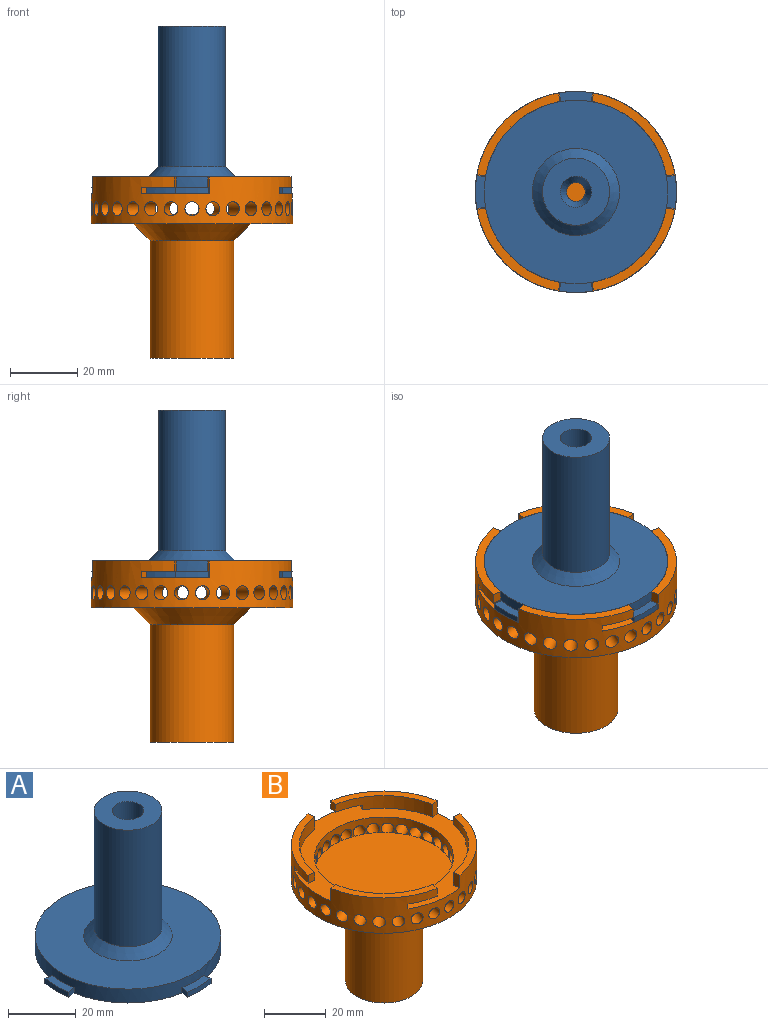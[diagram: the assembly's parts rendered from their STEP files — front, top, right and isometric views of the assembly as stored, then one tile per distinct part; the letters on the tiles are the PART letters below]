
ASSEMBLY  parts=2 mates=1
PART A: 27 faces, bbox 60x60x52.4 mm
  f0: plane 54.7x54.7mm, normal (0,0,1), area 1819.1mm2, adj f1,f26
  f1: cylinder r=27.35mm len=54.7mm, axis (0,0,-1), area 792.1mm2, adj f0,f9,f10,f11,f13,f15,f16,f17
  f2: cylinder r=4.65mm len=43.6mm, axis (0,0,-1), area 1273.7mm2, adj f4,f8
  f3: cylinder r=10mm len=42mm, axis (0,0,-1), area 2638.9mm2, adj f4,f26
  f4: plane 20x20mm, normal (0,0,1), area 246.2mm2, adj f2,f3
  f5: cylinder r=22.45mm len=44.9mm, axis (0,0,1), area 338.5mm2, adj f6,f9
  f6: plane 44.9x44.9mm, normal (0,0,-1), area 1558.7mm2, adj f5,f7
  f7: cylinder r=2.8mm len=5.6mm, axis (0,0,-1), area 80.9mm2, adj f6,f8
  f8: cone r=5mm half-angle=23.7deg, axis (0,0,1), area 107.5mm2, adj f2,f7
  f9: plane 60x60mm, normal (0,0,-1), area 867.4mm2, adj f1,f5,f10,f11,f12,f13,f14,f15
  f10: plane 2.61x1.85mm, normal (-0.17,0.99,0), area 4.9mm2, adj f1,f9,f12,f25
  f11: plane 2.61x1.85mm, normal (-0.17,-0.99,0), area 4.9mm2, adj f1,f9,f12,f25
  f12: cylinder r=30mm len=9.9mm, axis (0,0,1), area 18.4mm2, adj f9,f10,f11,f25
  f13: plane 2.61x1.85mm, normal (0.99,-0.17,0), area 4.9mm2, adj f1,f9,f14,f24
  f14: cylinder r=30mm len=9.9mm, axis (0,0,1), area 18.4mm2, adj f9,f13,f15,f24
  f15: plane 2.61x1.85mm, normal (-0.99,-0.17,0), area 4.9mm2, adj f1,f9,f14,f24
  f16: plane 2.61x1.85mm, normal (0.17,-0.99,0), area 4.9mm2, adj f1,f9,f18,f23
  f17: plane 2.61x1.85mm, normal (0.17,0.99,0), area 4.9mm2, adj f1,f9,f18,f23
  f18: cylinder r=30mm len=9.9mm, axis (0,0,1), area 18.4mm2, adj f9,f16,f17,f23
  f19: plane 2.61x1.85mm, normal (-0.99,0.17,0), area 4.9mm2, adj f1,f9,f20,f22
  f20: cylinder r=30mm len=9.9mm, axis (0,0,1), area 18.4mm2, adj f9,f19,f21,f22
  f21: plane 2.61x1.85mm, normal (0.99,0.17,0), area 4.9mm2, adj f1,f9,f20,f22
  f22: plane 9.9x3.03mm, normal (0,0,1), area 25.2mm2, adj f1,f19,f20,f21
  f23: plane 9.9x3.03mm, normal (0,0,1), area 25.2mm2, adj f1,f16,f17,f18
  f24: plane 9.9x3.03mm, normal (0,0,1), area 25.2mm2, adj f1,f13,f14,f15
  f25: plane 9.9x3.03mm, normal (0,0,1), area 25.2mm2, adj f1,f10,f11,f12
  f26: cone r=10mm half-angle=45deg, axis (0,0,-1), area 306.6mm2, adj f0,f3
PART B: 94 faces, bbox 60.1x60x54 mm
  f0: cylinder r=30mm len=60mm, axis (0,0,-1), area 1933mm2, adj f5,f6,f7,f8,f10,f11,f12,f13
  f1: cylinder r=27.4mm len=22.23mm, axis (0,0,-1), area 149.2mm2, adj f5,f8,f77,f83,f87,f88
  f2: cylinder r=27.4mm len=22.23mm, axis (0,0,-1), area 149.2mm2, adj f6,f8,f80,f81,f85,f86
  f3: cylinder r=27.4mm len=22.23mm, axis (0,0,-1), area 149.2mm2, adj f7,f8,f79,f84,f91,f92
  f4: cylinder r=27.4mm len=22.23mm, axis (0,0,-1), area 149.2mm2, adj f8,f76,f78,f82,f89,f90
  f5: plane 24.79x24.79mm, normal (0,0,1), area 91.2mm2, adj f0,f1,f77,f83
  f6: plane 24.79x24.79mm, normal (0,0,1), area 91.2mm2, adj f0,f2,f80,f81
  f7: plane 24.79x24.79mm, normal (0,0,1), area 91.2mm2, adj f0,f3,f79,f84
  f8: plane 60x60mm, normal (0,0,1), area 976.5mm2, adj f0,f1,f2,f3,f4,f9,f78,f79
  f9: cylinder r=22.5mm len=45mm, axis (0,0,1), area 475mm2, adj f8,f10,f11,f12,f13,f14,f15,f16
  f10: cylinder r=2.1mm len=8.31mm, axis (-0.21,-0.98,0), area 99.1mm2, adj f0,f9,f45
  f11: cylinder r=2.1mm len=8.65mm, axis (-0.41,-0.91,0), area 99.1mm2, adj f0,f9,f46
  f12: cylinder r=2.1mm len=8.62mm, axis (-0.59,-0.81,0), area 99.1mm2, adj f0,f9,f47
  f13: cylinder r=2.1mm len=8.46mm, axis (-0.74,-0.67,0), area 99.1mm2, adj f0,f9,f48
  f14: cylinder r=2.1mm len=8.68mm, axis (-0.87,-0.5,0), area 99.1mm2, adj f0,f9,f49
  f15: cylinder r=2.1mm len=8.52mm, axis (-0.95,-0.31,0), area 99.1mm2, adj f0,f9,f50
  f16: cylinder r=2.1mm len=8mm, axis (-0.99,-0.1,0), area 99.1mm2, adj f0,f9,f51
  f17: cylinder r=2.1mm len=8mm, axis (-0.99,0.1,0), area 99.1mm2, adj f0,f9,f52
  f18: cylinder r=2.1mm len=8.52mm, axis (-0.95,0.31,0), area 99.1mm2, adj f0,f9,f53
  f19: cylinder r=2.1mm len=8.68mm, axis (-0.87,0.5,0), area 99.1mm2, adj f0,f9,f54
  f20: cylinder r=2.1mm len=8.46mm, axis (-0.74,0.67,0), area 99.1mm2, adj f0,f9,f55
  f21: cylinder r=2.1mm len=8.62mm, axis (-0.59,0.81,0), area 99.1mm2, adj f0,f9,f56
  f22: cylinder r=2.1mm len=8.65mm, axis (-0.41,0.91,0), area 99.1mm2, adj f0,f9,f57
  f23: cylinder r=2.1mm len=8.31mm, axis (-0.21,0.98,0), area 99.1mm2, adj f0,f9,f58
  f24: cylinder r=2.1mm len=7.6mm, axis (0,1,0), area 99.1mm2, adj f0,f9,f59
  f25: cylinder r=2.1mm len=8.31mm, axis (0.21,0.98,0), area 99.1mm2, adj f0,f9,f60
  f26: cylinder r=2.1mm len=8.65mm, axis (0.41,0.91,0), area 99.1mm2, adj f0,f9,f61
  f27: cylinder r=2.1mm len=8.62mm, axis (0.59,0.81,0), area 99.1mm2, adj f0,f9,f62
  f28: cylinder r=2.1mm len=8.46mm, axis (0.74,0.67,0), area 99.1mm2, adj f0,f9,f63
  f29: cylinder r=2.1mm len=8.68mm, axis (0.87,0.5,0), area 99.1mm2, adj f0,f9,f64
  f30: cylinder r=2.1mm len=8.52mm, axis (0.95,0.31,0), area 99.1mm2, adj f0,f9,f65
  f31: cylinder r=2.1mm len=8mm, axis (0.99,0.1,0), area 99.1mm2, adj f0,f9,f66
  f32: cylinder r=2.1mm len=8mm, axis (0.99,-0.1,0), area 99.1mm2, adj f0,f9,f67
  f33: cylinder r=2.1mm len=8.52mm, axis (0.95,-0.31,0), area 99.1mm2, adj f0,f9,f68
  f34: cylinder r=2.1mm len=8.68mm, axis (0.87,-0.5,0), area 99.1mm2, adj f0,f9,f69
  f35: cylinder r=2.1mm len=8.46mm, axis (0.74,-0.67,0), area 99.1mm2, adj f0,f9,f70
  f36: cylinder r=2.1mm len=8.62mm, axis (0.59,-0.81,0), area 99.1mm2, adj f0,f9,f71
  f37: cylinder r=2.1mm len=8.65mm, axis (0.41,-0.91,0), area 99.1mm2, adj f0,f9,f72
  f38: cylinder r=2.1mm len=8.31mm, axis (0.21,-0.98,0), area 99.1mm2, adj f0,f9,f73
  f39: cylinder r=4.1mm len=30mm, axis (0,0,-1), area 772.8mm2, adj f41,f42
  f40: cylinder r=12.5mm len=35mm, axis (0,0,-1), area 2748.9mm2, adj f41,f93
  f41: plane 25x25mm, normal (0,0,-1), area 438.1mm2, adj f39,f40
  f42: plane 8.2x8.2mm, normal (0,0,-1), area 52.8mm2, adj f39
  f43: plane 60x60mm, normal (0,0,-1), area 1865.3mm2, adj f0,f93
  f44: cylinder r=2.1mm len=7.6mm, axis (0,-1,0), area 99.1mm2, adj f0,f9,f74
  f45: cylinder r=22.5mm len=2.6mm, axis (0,0,-1), area 0.9mm2, adj f10,f75
  f46: cylinder r=22.5mm len=2.43mm, axis (0,0,-1), area 0.9mm2, adj f11,f75
  f47: cylinder r=22.5mm len=2.15mm, axis (0,0,-1), area 0.9mm2, adj f12,f75
  f48: cylinder r=22.5mm len=1.98mm, axis (0,0,-1), area 0.9mm2, adj f13,f75
  f49: cylinder r=22.5mm len=2.3mm, axis (0,0,-1), area 0.9mm2, adj f14,f75
  f50: cylinder r=22.5mm len=2.53mm, axis (0,0,-1), area 0.9mm2, adj f15,f75
  f51: cylinder r=22.5mm len=2.65mm, axis (0,0,-1), area 0.9mm2, adj f16,f75
  f52: cylinder r=22.5mm len=2.65mm, axis (0,0,-1), area 0.9mm2, adj f17,f75
  f53: cylinder r=22.5mm len=2.53mm, axis (0,0,-1), area 0.9mm2, adj f18,f75
  f54: cylinder r=22.5mm len=2.3mm, axis (0,0,-1), area 0.9mm2, adj f19,f75
  f55: cylinder r=22.5mm len=1.98mm, axis (0,0,-1), area 0.9mm2, adj f20,f75
  f56: cylinder r=22.5mm len=2.15mm, axis (0,0,-1), area 0.9mm2, adj f21,f75
  f57: cylinder r=22.5mm len=2.43mm, axis (0,0,-1), area 0.9mm2, adj f22,f75
  f58: cylinder r=22.5mm len=2.6mm, axis (0,0,-1), area 0.9mm2, adj f23,f75
  f59: cylinder r=22.5mm len=2.66mm, axis (0,0,-1), area 0.9mm2, adj f24,f75
  f60: cylinder r=22.5mm len=2.6mm, axis (0,0,-1), area 0.9mm2, adj f25,f75
  f61: cylinder r=22.5mm len=2.43mm, axis (0,0,-1), area 0.9mm2, adj f26,f75
  f62: cylinder r=22.5mm len=2.15mm, axis (0,0,-1), area 0.9mm2, adj f27,f75
  f63: cylinder r=22.5mm len=1.98mm, axis (0,0,-1), area 0.9mm2, adj f28,f75
  f64: cylinder r=22.5mm len=2.3mm, axis (0,0,-1), area 0.9mm2, adj f29,f75
  f65: cylinder r=22.5mm len=2.53mm, axis (0,0,-1), area 0.9mm2, adj f30,f75
  f66: cylinder r=22.5mm len=2.65mm, axis (0,0,-1), area 0.9mm2, adj f31,f75
  f67: cylinder r=22.5mm len=2.65mm, axis (0,0,-1), area 0.9mm2, adj f32,f75
  f68: cylinder r=22.5mm len=2.53mm, axis (0,0,-1), area 0.9mm2, adj f33,f75
  f69: cylinder r=22.5mm len=2.3mm, axis (0,0,-1), area 0.9mm2, adj f34,f75
  f70: cylinder r=22.5mm len=1.98mm, axis (0,0,-1), area 0.9mm2, adj f35,f75
  f71: cylinder r=22.5mm len=2.15mm, axis (0,0,-1), area 0.9mm2, adj f36,f75
  f72: cylinder r=22.5mm len=2.43mm, axis (0,0,-1), area 0.9mm2, adj f37,f75
  f73: cylinder r=22.5mm len=2.6mm, axis (0,0,-1), area 0.9mm2, adj f38,f75
  f74: cylinder r=22.5mm len=2.66mm, axis (0,0,-1), area 0.9mm2, adj f44,f75
  f75: plane 45x45mm, normal (0,0,1), area 1590.4mm2, adj f9,f45,f46,f47,f48,f49,f50,f51
  f76: plane 24.79x24.79mm, normal (0,0,1), area 91.2mm2, adj f0,f4,f78,f82
  f77: plane 3.1x2.56mm, normal (0.98,-0.17,0), area 8.1mm2, adj f0,f1,f5,f88
  f78: plane 5x2.56mm, normal (-0.98,-0.17,0), area 13mm2, adj f0,f4,f8,f76
  f79: plane 5x2.56mm, normal (0.98,0.17,0), area 13mm2, adj f0,f3,f7,f8
  f80: plane 3.1x2.56mm, normal (-0.98,0.17,0), area 8.1mm2, adj f0,f2,f6,f86
  f81: plane 5x2.56mm, normal (0.17,-0.98,0), area 13mm2, adj f0,f2,f6,f8
  f82: plane 3.1x2.56mm, normal (0.17,0.98,0), area 8.1mm2, adj f0,f4,f76,f90
  f83: plane 5x2.56mm, normal (-0.17,0.98,0), area 13mm2, adj f0,f1,f5,f8
  f84: plane 3.1x2.56mm, normal (-0.17,-0.98,0), area 8.1mm2, adj f0,f3,f7,f92
  f85: plane 2.25x1.9mm, normal (-0.87,0.5,0), area 4.9mm2, adj f0,f2,f8,f86
  f86: plane 10.24x5.82mm, normal (0,0,-1), area 26mm2, adj f0,f2,f80,f85
  f87: plane 2.25x1.9mm, normal (0.87,-0.5,0), area 4.9mm2, adj f0,f1,f8,f88
  f88: plane 10.24x5.82mm, normal (0,0,-1), area 26mm2, adj f0,f1,f77,f87
  f89: plane 2.25x1.9mm, normal (0.5,0.87,0), area 4.9mm2, adj f0,f4,f8,f90
  f90: plane 10.24x5.82mm, normal (0,0,-1), area 26mm2, adj f0,f4,f82,f89
  f91: plane 2.25x1.9mm, normal (-0.5,-0.87,0), area 4.9mm2, adj f0,f3,f8,f92
  f92: plane 10.24x5.82mm, normal (0,0,-1), area 26mm2, adj f0,f3,f84,f91
  f93: cone r=17.5mm half-angle=45deg, axis (0,0,1), area 666.4mm2, adj f40,f43
PLACE A t=(25.36,35.02,7.32)mm
PLACE B t=(25.36,35.02,-41.68)mm
MATE fastened B.f0 <-> A.f1  axis (0,0,1) through (25.36,35.02,7.32)mm
